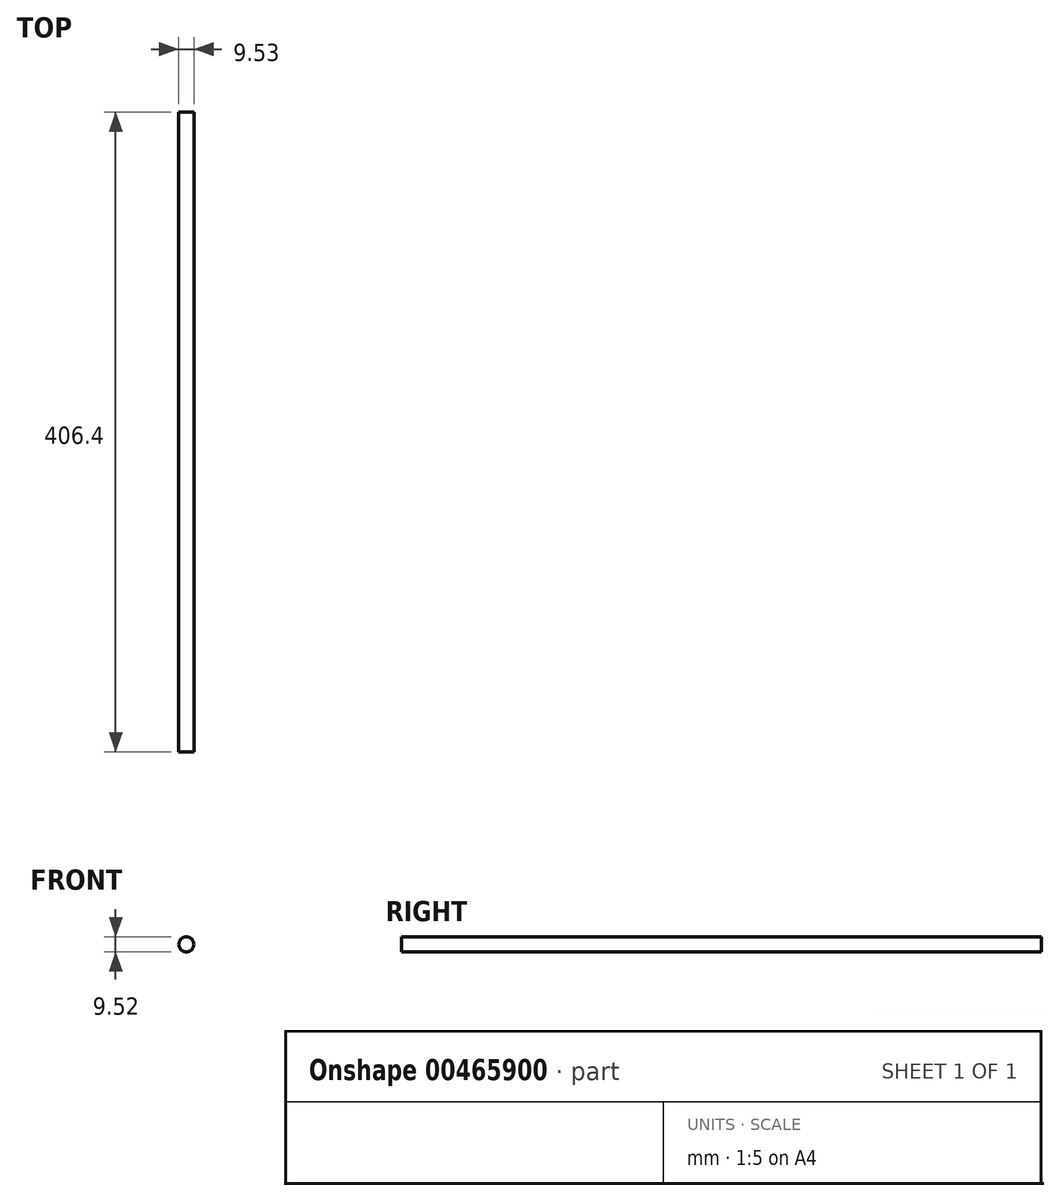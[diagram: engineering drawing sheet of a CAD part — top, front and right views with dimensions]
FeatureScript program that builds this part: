
annotation { "Feature Type Name" : "Feature", "Feature Type Description" : "" }
export const myFeature = defineFeature(function(context is Context, id is Id, definition is map)
    precondition{}
    {
        {
            var Q0;
            Q0=qCreatedBy(makeId("Front.planeOp"),FACE);
            var sketch = newSketch(context, id + "F0", { "sketchPlane" : qUnion([Q0])});
            skCircle(sketch, "E0", {"center": v(1.5, 0) * mm, "radius": 4.76 * mm});
            skSolve(sketch);
        }
        {
            var Q0;
            Q0=makeQuery(id+"F0.imprint","IMPRINT",FACE,{"disambiguationData":[TD([[makeQuery(id+"F0.imprint","IMPRINT",EDGE,{"derivedFrom":sQuery(id+"F0.wireOp",EDGE,"E0")}),1.0]])]});
            extrude(context, id + "F1", {"entities" : qUnion([Q0]), "depth" : 406.4 * mm});
        }
    });
